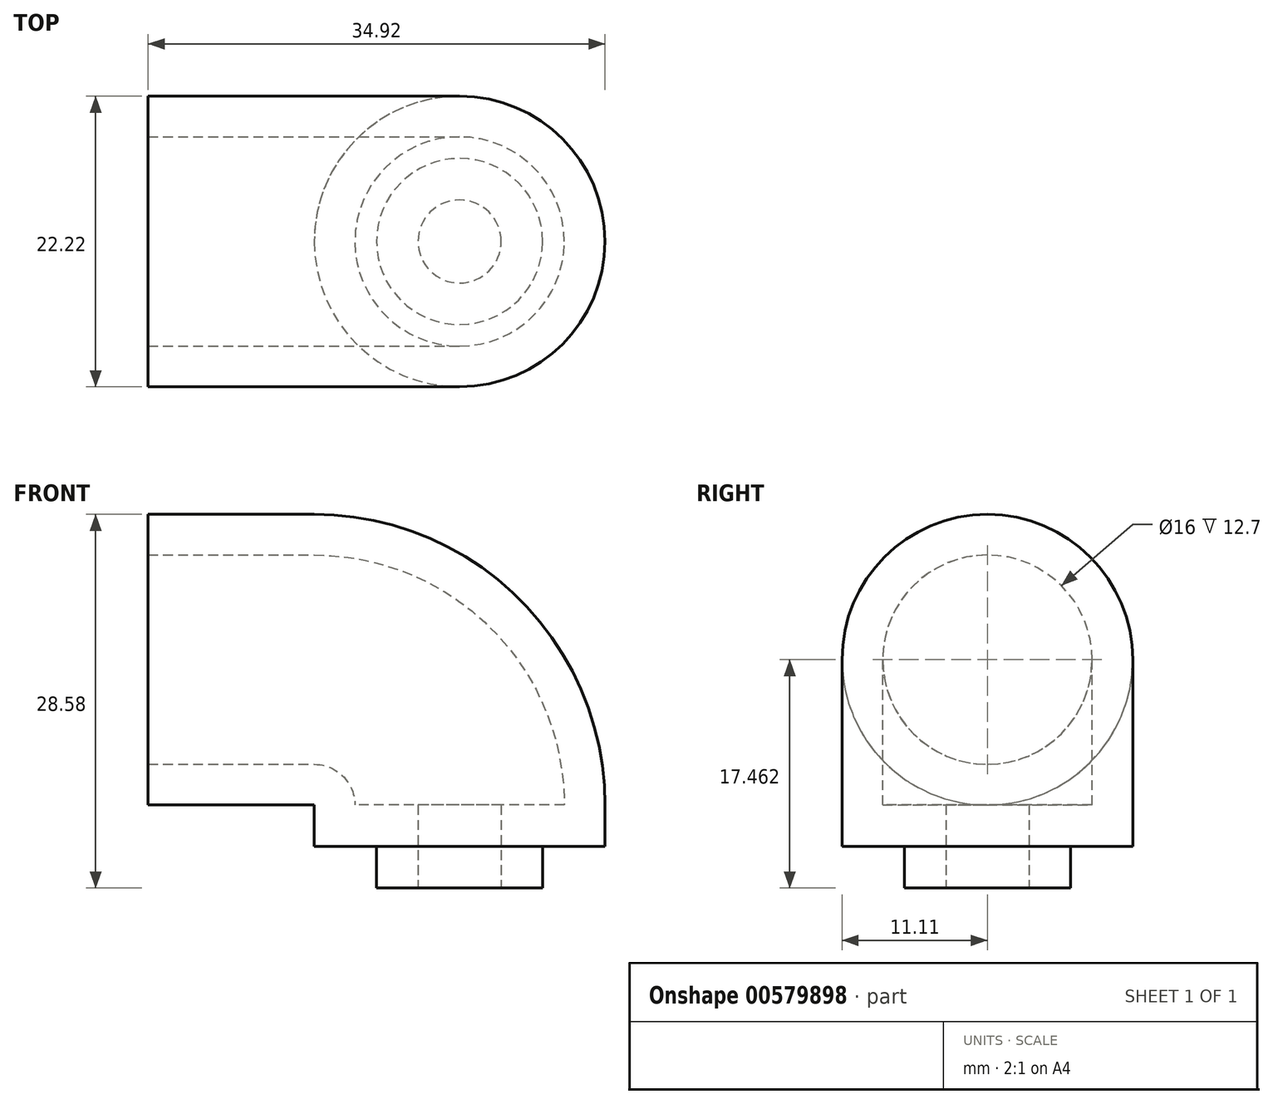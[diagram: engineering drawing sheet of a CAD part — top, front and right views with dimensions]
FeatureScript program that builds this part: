
annotation { "Feature Type Name" : "Feature", "Feature Type Description" : "" }
export const myFeature = defineFeature(function(context is Context, id is Id, definition is map)
    precondition{}
    {
        {
            var Q0;
            Q0=qCreatedBy(makeId("Top.planeOp"),FACE);
            var sketch = newSketch(context, id + "F0", { "sketchPlane" : qUnion([Q0])});
            skCircle(sketch, "E0", {"center": v(0, 0) * mm, "radius": 3.18 * mm});
            skCircle(sketch, "E1", {"center": v(0, 0) * mm, "radius": 6.35 * mm});
            skSolve(sketch);
        }
        {
            var Q0;
            Q0 = qSketchRegion(id + "F0", true);
            extrude(context, id + "F1", {"entities" : qUnion([Q0]), "depth" : 3.17 * mm, "offsetDistance" : 25.4 * mm});
        }
        {
            var Q0;
            Q0=makeQuery(id+"F1.opExtrude","CAP_FACE",FACE,{"disambiguationData":[OSD([sQuery(id+"F0.wireOp",EDGE,"E0"),sQuery(id+"F0.wireOp",EDGE,"E1")])],"isStart":false});
            var sketch = newSketch(context, id + "F2", { "sketchPlane" : qUnion([Q0])});
            skCircle(sketch, "E2", {"center": v(0, 0) * mm, "radius": 11.11 * mm});
            skCircle(sketch, "E3", {"center": v(0, 0) * mm, "radius": 3.18 * mm});
            skSolve(sketch);
        }
        {
            var Q0;
            Q0 = qSketchRegion(id + "F2", true);
            extrude(context, id + "F3", {"entities" : qUnion([Q0]), "operationType" : NewBodyOperationType.ADD, "depth" : 3.17 * mm, "offsetDistance" : 25.4 * mm});
        }
        {
            var Q0;
            Q0=makeQuery(id+"F3.opExtrude","CAP_FACE",FACE,{"disambiguationData":[OSD([sQuery(id+"F2.wireOp",EDGE,"E2"),sQuery(id+"F2.wireOp",EDGE,"E3")])],"isStart":false});
            var sketch = newSketch(context, id + "F4", { "sketchPlane" : qUnion([Q0])});
            skCircle(sketch, "E4", {"center": v(0, 0) * mm, "radius": 8 * mm});
            skCircle(sketch, "E5", {"center": v(0, 0) * mm, "radius": 11.11 * mm});
            skLineSegment(sketch, "E6", {"start": v(-11.11, 9.62) * mm, "end": v(-11.11, -13.9) * mm});
            skSolve(sketch);
        }
        {
            var Q0;
            Q0 = qSketchRegion(id + "F4", true);
            var Q1;
            Q1=sQuery(id+"F4.wireOp",EDGE,"E6");
            revolve(context, id + "F5", {"operationType" : NewBodyOperationType.ADD, "entities" : qUnion([Q0]), "axis" : qUnion([Q1]), "revolveType" : RevolveType.ONE_DIRECTION, "angle" : 90 * degree});
        }
        {
            var Q0;
            Q0=makeQuery(id+"F5.opRevolve","CAP_FACE",FACE,{"disambiguationData":[OSD([sQuery(id+"F4.wireOp",EDGE,"E4"),sQuery(id+"F4.wireOp",EDGE,"E5")])],"isStart":false});
            var sketch = newSketch(context, id + "F6", { "sketchPlane" : qUnion([Q0])});
            skCircle(sketch, "E7", {"center": v(0, 17.46) * mm, "radius": 8 * mm});
            skCircle(sketch, "E8", {"center": v(0, 17.46) * mm, "radius": 11.11 * mm});
            skSolve(sketch);
        }
        {
            var Q0;
            Q0 = qSketchRegion(id + "F6", true);
            extrude(context, id + "F7", {"entities" : qUnion([Q0]), "operationType" : NewBodyOperationType.ADD, "depth" : 12.7 * mm, "offsetDistance" : 25.4 * mm});
        }
    });
